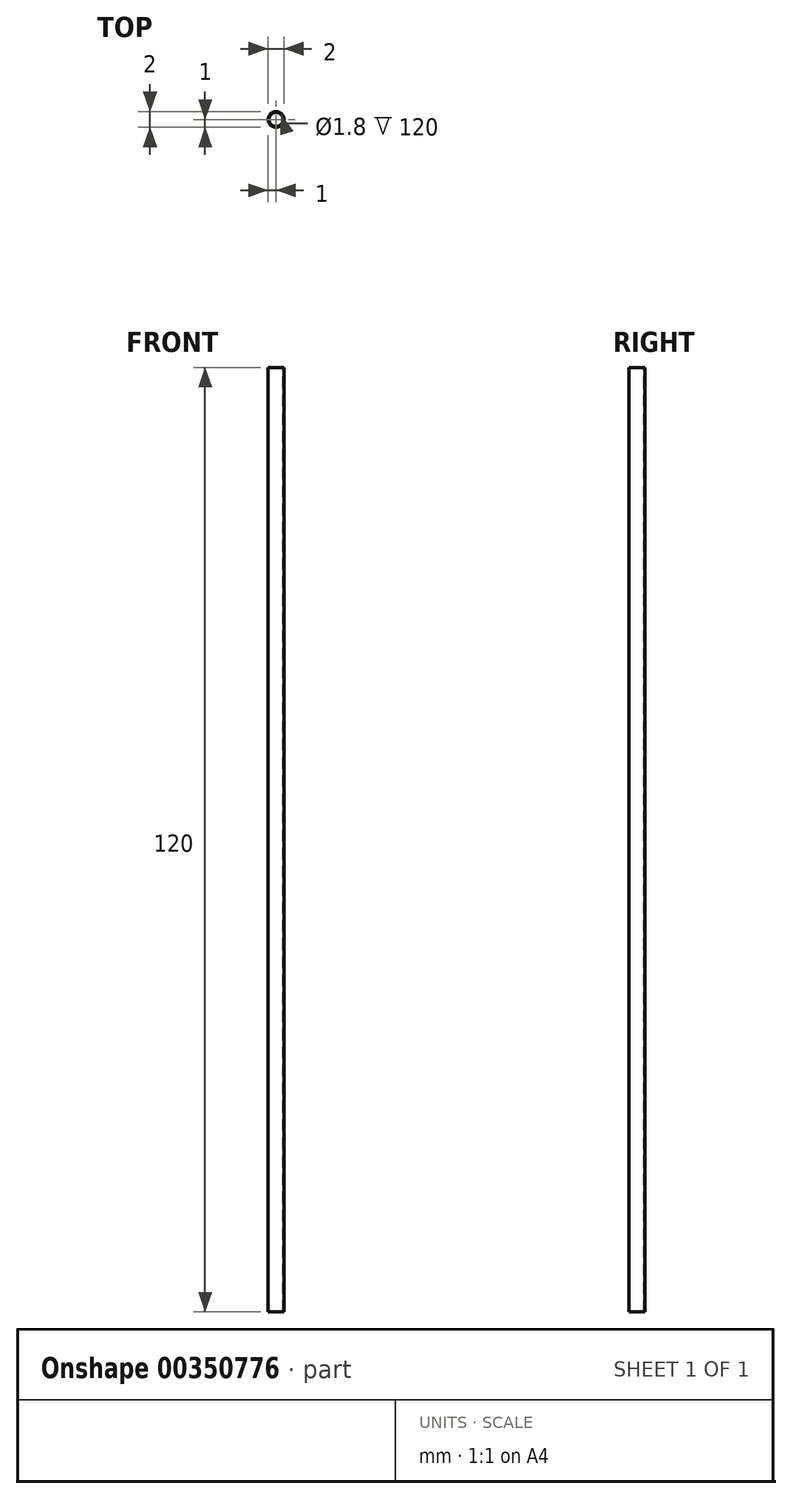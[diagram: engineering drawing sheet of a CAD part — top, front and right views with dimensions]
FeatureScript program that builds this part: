
annotation { "Feature Type Name" : "Feature", "Feature Type Description" : "" }
export const myFeature = defineFeature(function(context is Context, id is Id, definition is map)
    precondition{}
    {
        {
            var Q0;
            Q0=qCreatedBy(makeId("Top.planeOp"),FACE);
            var sketch = newSketch(context, id + "F0", { "sketchPlane" : qUnion([Q0])});
            skLineSegment(sketch, "E0.bottom", {"start": v(167.1, 194) * mm, "end": v(-167.1, 194) * mm});
            skLineSegment(sketch, "E0.top", {"start": v(167.1, -194) * mm, "end": v(-167.1, -194) * mm});
            skLineSegment(sketch, "E0.left", {"start": v(167.1, 194) * mm, "end": v(167.1, -194) * mm});
            skLineSegment(sketch, "E0.right", {"start": v(-167.1, 194) * mm, "end": v(-167.1, -194) * mm});
            skPoint(sketch, "E0.middle", {"position": v(0, 0) * mm});
            skLineSegment(sketch, "E1", {"start": v(-167.1, 194) * mm, "end": v(-167.1, 0) * mm});
            skLineSegment(sketch, "E2", {"start": v(-167.1, 0) * mm, "end": v(-167.1, -194) * mm});
            skLineSegment(sketch, "E3", {"start": v(167.1, -194) * mm, "end": v(167.1, 0) * mm});
            skLineSegment(sketch, "E4", {"start": v(167.1, 0) * mm, "end": v(167.1, 194) * mm});
            skLineSegment(sketch, "E5", {"start": v(-167.1, 0) * mm, "end": v(167.1, 0) * mm});
            skLineSegment(sketch, "E6", {"start": v(-161.1, -188) * mm, "end": v(-161.1, 189) * mm});
            skLineSegment(sketch, "E7", {"start": v(-161.1, 189) * mm, "end": v(162.1, 189) * mm});
            skLineSegment(sketch, "E8", {"start": v(162.1, 189) * mm, "end": v(162.1, -188) * mm});
            skLineSegment(sketch, "E9", {"start": v(162.1, -188) * mm, "end": v(-161.1, -188) * mm});
            skLineSegment(sketch, "E10", {"start": v(-167.1, 0) * mm, "end": v(-161.1, 0) * mm});
            skLineSegment(sketch, "E11", {"start": v(-161.1, 0) * mm, "end": v(162.1, 0) * mm});
            skLineSegment(sketch, "E12", {"start": v(162.1, 0) * mm, "end": v(167.1, 0) * mm});
            skLineSegment(sketch, "E13", {"start": v(164.6, 0) * mm, "end": v(-164.1, 0) * mm});
            skLineSegment(sketch, "E14.bottom", {"start": v(-157.1, 50) * mm, "end": v(-171.1, 50) * mm});
            skLineSegment(sketch, "E14.top", {"start": v(-157.1, -50) * mm, "end": v(-171.1, -50) * mm});
            skLineSegment(sketch, "E14.left", {"start": v(-157.1, 50) * mm, "end": v(-157.1, -50) * mm});
            skLineSegment(sketch, "E14.right", {"start": v(-171.1, 50) * mm, "end": v(-171.1, -50) * mm});
            skPoint(sketch, "E14.middle", {"position": v(-164.1, 0) * mm});
            skLineSegment(sketch, "E15.bottom", {"start": v(171.1, 50) * mm, "end": v(158.1, 50) * mm});
            skLineSegment(sketch, "E15.top", {"start": v(171.1, -50) * mm, "end": v(158.1, -50) * mm});
            skLineSegment(sketch, "E15.left", {"start": v(171.1, 50) * mm, "end": v(171.1, -50) * mm});
            skLineSegment(sketch, "E15.right", {"start": v(158.1, 50) * mm, "end": v(158.1, -50) * mm});
            skPoint(sketch, "E15.middle", {"position": v(164.6, 0) * mm});
            skLineSegment(sketch, "E16.bottom", {"start": v(158.1, 5) * mm, "end": v(162.1, 5) * mm});
            skLineSegment(sketch, "E16.top", {"start": v(158.1, -5) * mm, "end": v(162.1, -5) * mm});
            skLineSegment(sketch, "E16.left", {"start": v(158.1, 5) * mm, "end": v(158.1, -5) * mm});
            skLineSegment(sketch, "E16.right", {"start": v(162.1, 5) * mm, "end": v(162.1, -5) * mm});
            skLineSegment(sketch, "E17.bottom", {"start": v(-157.1, 5) * mm, "end": v(-161.1, 5) * mm});
            skLineSegment(sketch, "E17.top", {"start": v(-157.1, -5) * mm, "end": v(-161.1, -5) * mm});
            skLineSegment(sketch, "E17.left", {"start": v(-157.1, 5) * mm, "end": v(-157.1, -5) * mm});
            skLineSegment(sketch, "E17.right", {"start": v(-161.1, 5) * mm, "end": v(-161.1, -5) * mm});
            skSolve(sketch);
        }
        {
            var Q0;
            Q0=qCreatedBy(makeId("Front.planeOp"),FACE);
            cPlane(context, id + "F1", {"entities" : qUnion([Q0]), "cplaneType" : CPlaneType.OFFSET, "offset" : 5 * mm, "oppositeDirection" : true, "width" : 150 * mm, "height" : 150 * mm});
        }
        {
            var Q0;
            Q0=qCreatedBy(makeId("Top.planeOp"),FACE);
            cPlane(context, id + "F2", {"entities" : qUnion([Q0]), "cplaneType" : CPlaneType.OFFSET, "offset" : 10 * mm, "width" : 150 * mm, "height" : 150 * mm});
        }
        {
            var Q0;
            Q0=qCreatedBy(id+"F2.planeOp",FACE);
            var sketch = newSketch(context, id + "F3", { "sketchPlane" : qUnion([Q0])});
            skLineSegment(sketch, "E18", {"start": v(0, 0) * mm, "end": v(0, 20) * mm});
            skCircle(sketch, "E19", {"center": v(0, 20) * mm, "radius": 1 * mm});
            skCircle(sketch, "E20", {"center": v(0, 20) * mm, "radius": 0.9 * mm});
            skSolve(sketch);
        }
        {
            var Q0;
            Q0=makeQuery(id+"F3.imprint","IMPRINT",FACE,{"disambiguationData":[TD([[makeQuery(id+"F3.imprint","IMPRINT",EDGE,{"derivedFrom":sQuery(id+"F3.wireOp",EDGE,"E19")}),1.0]])]});
            extrude(context, id + "F4", {"entities" : qUnion([Q0]), "oppositeDirection" : true, "depth" : 120 * mm});
        }
    });
